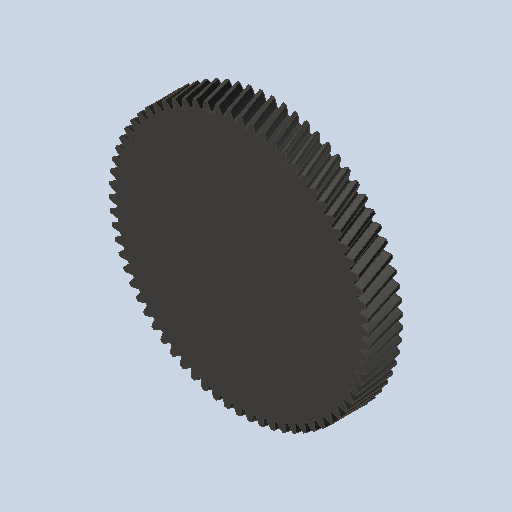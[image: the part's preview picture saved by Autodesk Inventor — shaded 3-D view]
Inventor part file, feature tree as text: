
AUTODESK INVENTOR PART (.ipt)
format: ipt  version: 2023 (Build 270158000, 158)  size: 899,072 bytes
history: native  units: mm (DEFAULTED — no unit token found)
features: plane x3, other x3, sketch x2, extrude x1
ambient origin geometry x8: Origin, YZ Plane, XZ Plane, XY Plane, X Axis, Y Axis, Z Axis, Center Point
bodies: Solid1 (feature_tree)
feature tree (9):
  extrude  "Extrusion1"  Depth=10.0mm TaperAngle=0.0deg
  plane  "Work Plane2"
  plane  "Work Plane8"
  plane  "Work Plane9"
  other  "Spur Gear"
  sketch  "Sketch1"  dims[d0=76.492444mm d1=10.0mm d2=0.0mm]
  sketch  "Sketch2"  dims[d3=74.492444mm d4=10.0mm d5=0.0mm d16=80.0mm d17=0.0mm d34=0.448799mm d39=0.0mm d41=0.0mm d43=80.0mm d46=80.0mm d47=0.0mm d48=0.0mm]
  other  "Srf1"
  other  "Pitch Diameter"
